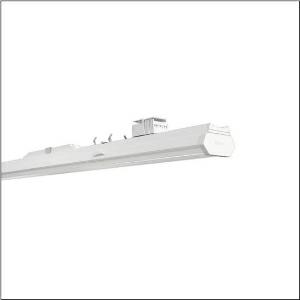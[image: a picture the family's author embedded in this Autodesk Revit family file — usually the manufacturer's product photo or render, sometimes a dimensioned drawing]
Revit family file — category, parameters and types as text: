
# Revit family: licross_r__11_protected_mo_51tp127n58xf_03c6
name_source: partatom
category: Lighting Fixtures
units: mm (PartAtom-declared; Revit-internal decimal feet)

## family parameters
Cut with Voids When Loaded = No
Host = Face
Light Source = No
Part Type = Normal
Room Calculation Point = No
Round Connector Dimension = Use Diameter
Shared = No

## types (1)
- Licross® 11 Protected MO (1 x LED, 8120 lm, 47.6 W, 5000K)
    Apparent Load = 48 VA
    CIE Flux Codes = 73 92 98 99 100
    Color Rendering = 80
    Color Temperature = 5000K
    Default Elevation = 1800 mm
    Description = Licross® 11 Protected MO, luminaire insert, of sheet steel, galvanised, coil coated, white, length: 1.500mm, width: 90mm, height: 101mm, LED rated luminous flux: 8.120lm, light colour: 850, control gear: ON/OFF, control gear: ECG, with plug, 3-pole, with phase selection, mains connection: 220..240V, AC, 50/60Hz, rated input power: 48W, halogen-free wiring, primary optical cover: cover, of PMMA, light emission: direct distribution, primary light characteristic: symmetric, protection rating (complete): IP64, insulation class (complete): insulation class I (protective earthing), certification: CE, ENEC, VDE, UKCA, protection symbol: D if used in an environment with conductive dust loads with corresponding accessories, impact resistance: IK06, permissible ambient temperature for indoor applications: -35..+45°C, reducing of maximum allowable ambient temperature of 5°C with ceiling mounting, corresponds to IFS (International Featured Standards) requirements for safety and quality in the food industry, LABS conformity tested according to VDMA 24364:2018-05, packaging unit: 1 piece
    Height = 92 mm
    Lamp = 1 x LED
    Lamp Light Flux = 8120 lm
    Lamp Power = 47.6 W
    Lamp count = 1
    Length = 1500 mm
    Luminous efficacy = 171 lm/W
    Manufacturer = Siteco
    ModVariant = No
    Model = 51TP127N58XF
    Mounting Place = Ceiling
    Mounting Type = Pendant
    Number of Poles = 1
    OnlyDefault = Yes
    Power Factor = 1
    Product Name = Licross® 11 Protected MO
    Product group = luminaire insert
    ProductGroupID = 902
    Protection Class = Protection class I
    Protection Degree = IP 64
    RLX_Detail_Level = 1
    RLX_Emergency_Light_Flux = 0 lm
    RLX_Emergency_Type = 0
    RLX_Emergency_Type_DB = No
    RlxData = <blob elided: 20621 chars, md5=13bb870b>
    Socket = socket
    Standby Power = 0 W
    System Light Flux = 8120 lm
    System Power = 48 W
    Type Comments = Product without accessories
    Type Image = l_1256148.jpg
    URL = http://relux.com
    VarID = ---
    Voltage = 0 V
    Weight = 0.00 kg
    Width = 88 mm

## geometry (parser evidence)
native form markers: Blend x4, Sweep x10
no freeform markers — native parametric forms only
